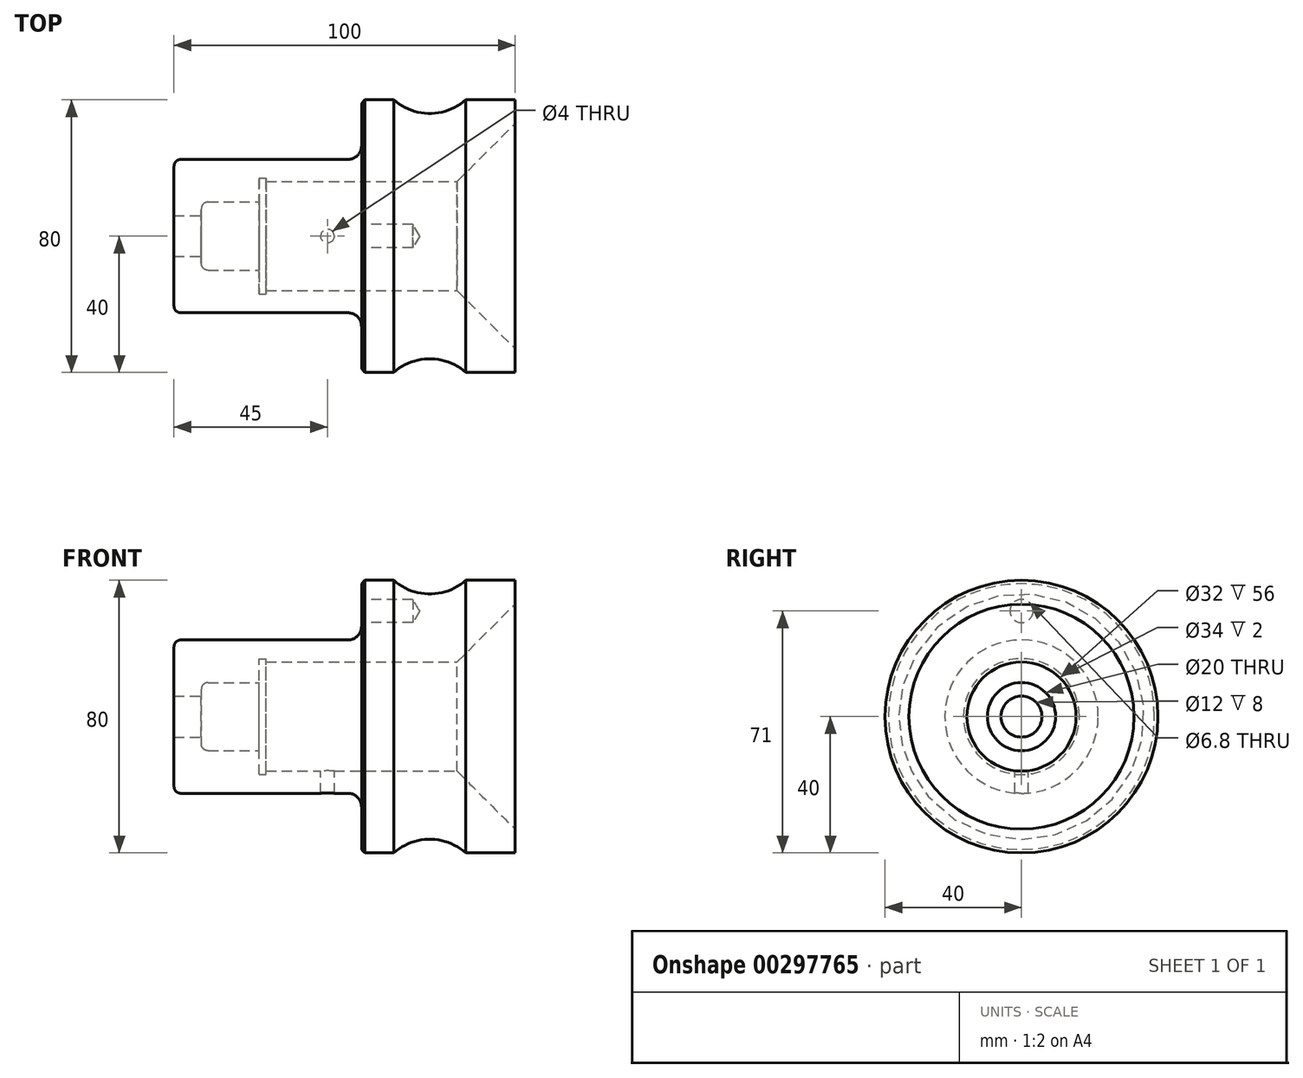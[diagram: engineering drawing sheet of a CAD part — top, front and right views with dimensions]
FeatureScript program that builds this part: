
annotation { "Feature Type Name" : "Feature", "Feature Type Description" : "" }
export const myFeature = defineFeature(function(context is Context, id is Id, definition is map)
    precondition{}
    {
        {
            var Q0;
            Q0=qCreatedBy(makeId("Front.planeOp"),FACE);
            var sketch = newSketch(context, id + "F0", { "sketchPlane" : qUnion([Q0])});
            skLineSegment(sketch, "E0", {"start": v(0, 0) * mm, "end": v(0, 40) * mm});
            skLineSegment(sketch, "E1", {"start": v(0, 40) * mm, "end": v(-45, 40) * mm});
            skLineSegment(sketch, "E2", {"start": v(-45, 40) * mm, "end": v(-45, 22.5) * mm});
            skLineSegment(sketch, "E3", {"start": v(-45, 22.5) * mm, "end": v(-100, 22.5) * mm});
            skLineSegment(sketch, "E4", {"start": v(-100, 22.5) * mm, "end": v(-100, 0) * mm});
            skLineSegment(sketch, "E5", {"start": v(-100, 0) * mm, "end": v(0, 0) * mm});
            skSolve(sketch);
        }
        {
            var Q0;
            Q0=makeQuery(id+"F0.imprint","IMPRINT",FACE,{"disambiguationData":[TD([[makeQuery(id+"F0.imprint","IMPRINT",EDGE,{"derivedFrom":sQuery(id+"F0.wireOp",EDGE,"E0")}),1.0]])]});
            var Q1;
            Q1=sQuery(id+"F0.wireOp",EDGE,"E5");
            revolve(context, id + "F1", {"entities" : qUnion([Q0]), "axis" : qUnion([Q1]), "revolveType" : RevolveType.FULL});
        }
        {
            var Q0;
            Q0=qCreatedBy(makeId("Front.planeOp"),FACE);
            var sketch = newSketch(context, id + "F2", { "sketchPlane" : qUnion([Q0])});
            skLineSegment(sketch, "E6", {"start": v(0, 0) * mm, "end": v(0, 33) * mm});
            skLineSegment(sketch, "E7", {"start": v(0, 33) * mm, "end": v(-17, 16) * mm});
            skLineSegment(sketch, "E8", {"start": v(-17, 16) * mm, "end": v(-73, 16) * mm});
            skLineSegment(sketch, "E9", {"start": v(-73, 16) * mm, "end": v(-73, 17) * mm});
            skLineSegment(sketch, "E10", {"start": v(-73, 17) * mm, "end": v(-75, 17) * mm});
            skLineSegment(sketch, "E11", {"start": v(-75, 17) * mm, "end": v(-75, 10) * mm});
            skLineSegment(sketch, "E12", {"start": v(-75, 10) * mm, "end": v(-92, 10) * mm});
            skLineSegment(sketch, "E13", {"start": v(-92, 10) * mm, "end": v(-92, 6) * mm});
            skLineSegment(sketch, "E14", {"start": v(-92, 6) * mm, "end": v(-100, 6) * mm});
            skLineSegment(sketch, "E15", {"start": v(-100, 6) * mm, "end": v(-100, 0) * mm});
            skLineSegment(sketch, "E16", {"start": v(-100, 0) * mm, "end": v(0, 0) * mm});
            skSolve(sketch);
        }
        {
            var Q0;
            Q0 = qSketchRegion(id + "F2", true);
            var Q1;
            Q1=sQuery(id+"F2.wireOp",EDGE,"E16");
            revolve(context, id + "F3", {"operationType" : NewBodyOperationType.REMOVE, "entities" : qUnion([Q0]), "axis" : qUnion([Q1]), "revolveType" : RevolveType.FULL, "oppositeDirection" : true});
        }
        {
            var Q0;
            Q0=qCreatedBy(makeId("Front.planeOp"),FACE);
            var sketch = newSketch(context, id + "F4", { "sketchPlane" : qUnion([Q0])});
            skCircle(sketch, "E17", {"center": v(-25, 52) * mm, "radius": 16 * mm});
            skSolve(sketch);
        }
        {
            var Q0;
            Q0=makeQuery(id+"F4.imprint","IMPRINT",FACE,{"disambiguationData":[TD([[makeQuery(id+"F4.imprint","IMPRINT",EDGE,{"derivedFrom":sQuery(id+"F4.wireOp",EDGE,"E17")}),1.0]])]});
            var Q1;
            Q1=sQuery(id+"F0.wireOp",EDGE,"E5");
            revolve(context, id + "F5", {"operationType" : NewBodyOperationType.REMOVE, "entities" : qUnion([Q0]), "axis" : qUnion([Q1]), "revolveType" : RevolveType.FULL, "oppositeDirection" : true});
        }
        {
            var Q0;
            Q0=qCreatedBy(makeId("Top.planeOp"),FACE);
            var sketch = newSketch(context, id + "F6", { "sketchPlane" : qUnion([Q0])});
            skCircle(sketch, "E18", {"center": v(-55, 0) * mm, "radius": 2 * mm});
            skSolve(sketch);
        }
        {
            var Q0;
            Q0 = qSketchRegion(id + "F6", true);
            extrude(context, id + "F7", {"entities" : qUnion([Q0]), "operationType" : NewBodyOperationType.REMOVE, "endBound" : BoundingType.THROUGH_ALL, "oppositeDirection" : true, "depth" : 25 * mm});
        }
        {
            var Q0;
            Q0=makeQuery(id+"F1.opRevolve","SWEPT_FACE",FACE,{"disambiguationData":[OSD([sQuery(id+"F0.wireOp",EDGE,"E2")])]});
            var sketch = newSketch(context, id + "F8", { "sketchPlane" : qUnion([Q0])});
            skPoint(sketch, "E19", {"position": v(0, 31) * mm});
            skSolve(sketch);
        }
        {
            var Q0;
            Q0=sQuery(id+"F8.wireOp",VERTEX,"E19");
            var Q1;
            Q1=makeQuery(id+"F1.opRevolve","SWEPT_BODY",BODY,{"disambiguationData":[OSD([sQuery(id+"F0.wireOp",EDGE,"E0"),sQuery(id+"F0.wireOp",EDGE,"E1"),sQuery(id+"F0.wireOp",EDGE,"E2"),sQuery(id+"F0.wireOp",EDGE,"E3"),sQuery(id+"F0.wireOp",EDGE,"E4"),sQuery(id+"F0.wireOp",EDGE,"E5")])]});
            hole(context, id + "F9", {"style" : HoleStyle.SIMPLE, "endStyle" : HoleEndStyle.BLIND, "standardTappedOrClearance" : lookupTablePath({ "standard" : "ISO", "engagement" : "75%", "pitch" : "1.25 mm", "size" : "M8", "type" : "Tapped" }), "standardBlindInLast" : lookupTablePath({ "standard" : "ISO", "engagement" : "75%", "pitch" : "1.25 mm", "size" : "M8", "type" : "Tapped" }), "holeDiameter" : 6.8 * mm, "showTappedDepth" : true, "holeDepth" : 15 * mm, "tappedDepth" : 10 * mm, "tapClearance" : 4, "locations" : qUnion([Q0]), "scope" : qUnion([Q1]), "majorDiameter" : 8 * mm});
        }
        {
            var Q0;
            Q0=makeQuery(id+"F1.opRevolve","SWEPT_EDGE",EDGE,{"disambiguationData":[OSD([sQuery(id+"F0.wireOp",EDGE,"E1"),sQuery(id+"F0.wireOp",EDGE,"E2")])]});
            chamfer(context, id + "F10", {"entities" : qUnion([Q0]), "width" : 1 * mm, "tangentPropagation" : true});
        }
        {
            var Q0;
            Q0=makeQuery(id+"F1.opRevolve","SWEPT_EDGE",EDGE,{"disambiguationData":[OSD([sQuery(id+"F0.wireOp",EDGE,"E3"),sQuery(id+"F0.wireOp",EDGE,"E4")])]});
            var Q1;
            Q1=makeQuery(id+"F3.boolean.opBoolean","COPY",EDGE,{"derivedFrom":makeQuery(id+"F3.opRevolve","SWEPT_EDGE",EDGE,{"disambiguationData":[OSD([sQuery(id+"F2.wireOp",EDGE,"E12"),sQuery(id+"F2.wireOp",EDGE,"E13")])]})});
            fillet(context, id + "F11", {"entities" : qUnion([Q0, Q1]), "radius" : 2 * mm, "tangentPropagation" : true, "allowEdgeOverflow" : false});
        }
        {
            var Q0;
            Q0=makeQuery(id+"F1.opRevolve","SWEPT_EDGE",EDGE,{"disambiguationData":[OSD([sQuery(id+"F0.wireOp",EDGE,"E2"),sQuery(id+"F0.wireOp",EDGE,"E3")])]});
            fillet(context, id + "F12", {"entities" : qUnion([Q0]), "radius" : 4 * mm, "tangentPropagation" : true, "allowEdgeOverflow" : false});
        }
    });
